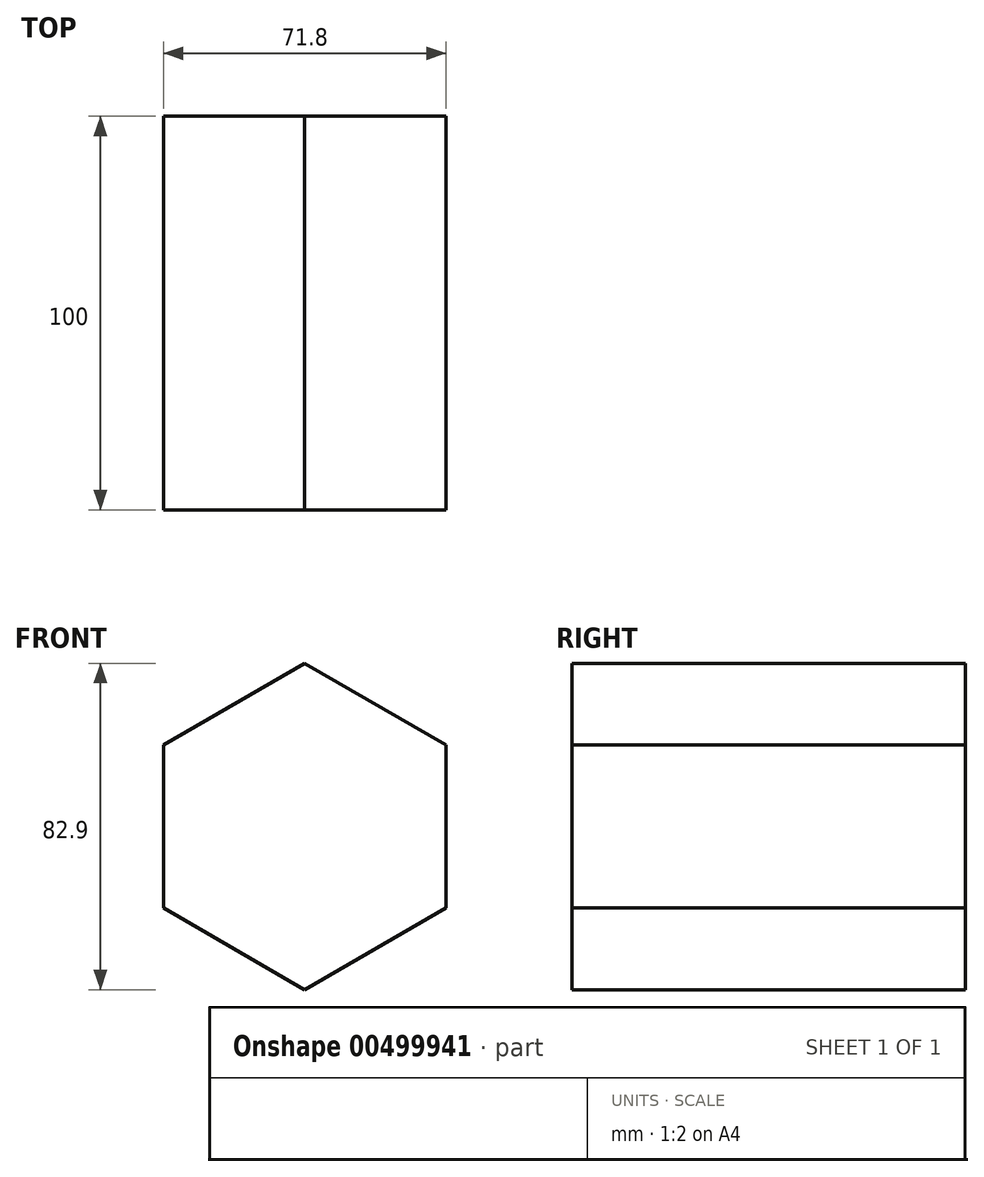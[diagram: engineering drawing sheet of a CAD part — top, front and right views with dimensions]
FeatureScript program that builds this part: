
annotation { "Feature Type Name" : "Feature", "Feature Type Description" : "" }
export const myFeature = defineFeature(function(context is Context, id is Id, definition is map)
    precondition{}
    {
        {
            var Q0;
            Q0=qCreatedBy(makeId("Front.planeOp"),FACE);
            var sketch = newSketch(context, id + "F0", { "sketchPlane" : qUnion([Q0])});
            skCircle(sketch, "E0.cCircle", {"center": v(0, 0) * mm, "radius": 41.45 * mm, "construction": true});
            skLineSegment(sketch, "E0.0", {"start": v(0, 41.45) * mm, "end": v(35.9, 20.73) * mm});
            skLineSegment(sketch, "E0.1", {"start": v(35.9, 20.73) * mm, "end": v(35.9, -20.73) * mm});
            skLineSegment(sketch, "E0.2", {"start": v(35.9, -20.73) * mm, "end": v(0, -41.45) * mm});
            skLineSegment(sketch, "E0.3", {"start": v(0, -41.45) * mm, "end": v(-35.9, -20.73) * mm});
            skLineSegment(sketch, "E0.4", {"start": v(-35.9, -20.73) * mm, "end": v(-35.9, 20.73) * mm});
            skLineSegment(sketch, "E0.5", {"start": v(-35.9, 20.73) * mm, "end": v(0, 41.45) * mm});
            skSolve(sketch);
        }
        {
            var Q0;
            Q0=makeQuery(id+"F0.imprint","IMPRINT",FACE,{"disambiguationData":[TD([[makeQuery(id+"F0.imprint","IMPRINT",EDGE,{"derivedFrom":sQuery(id+"F0.wireOp",EDGE,"E0.0")}),-1.0]])]});
            extrude(context, id + "F1", {"entities" : qUnion([Q0]), "depth" : 100 * mm});
        }
    });
